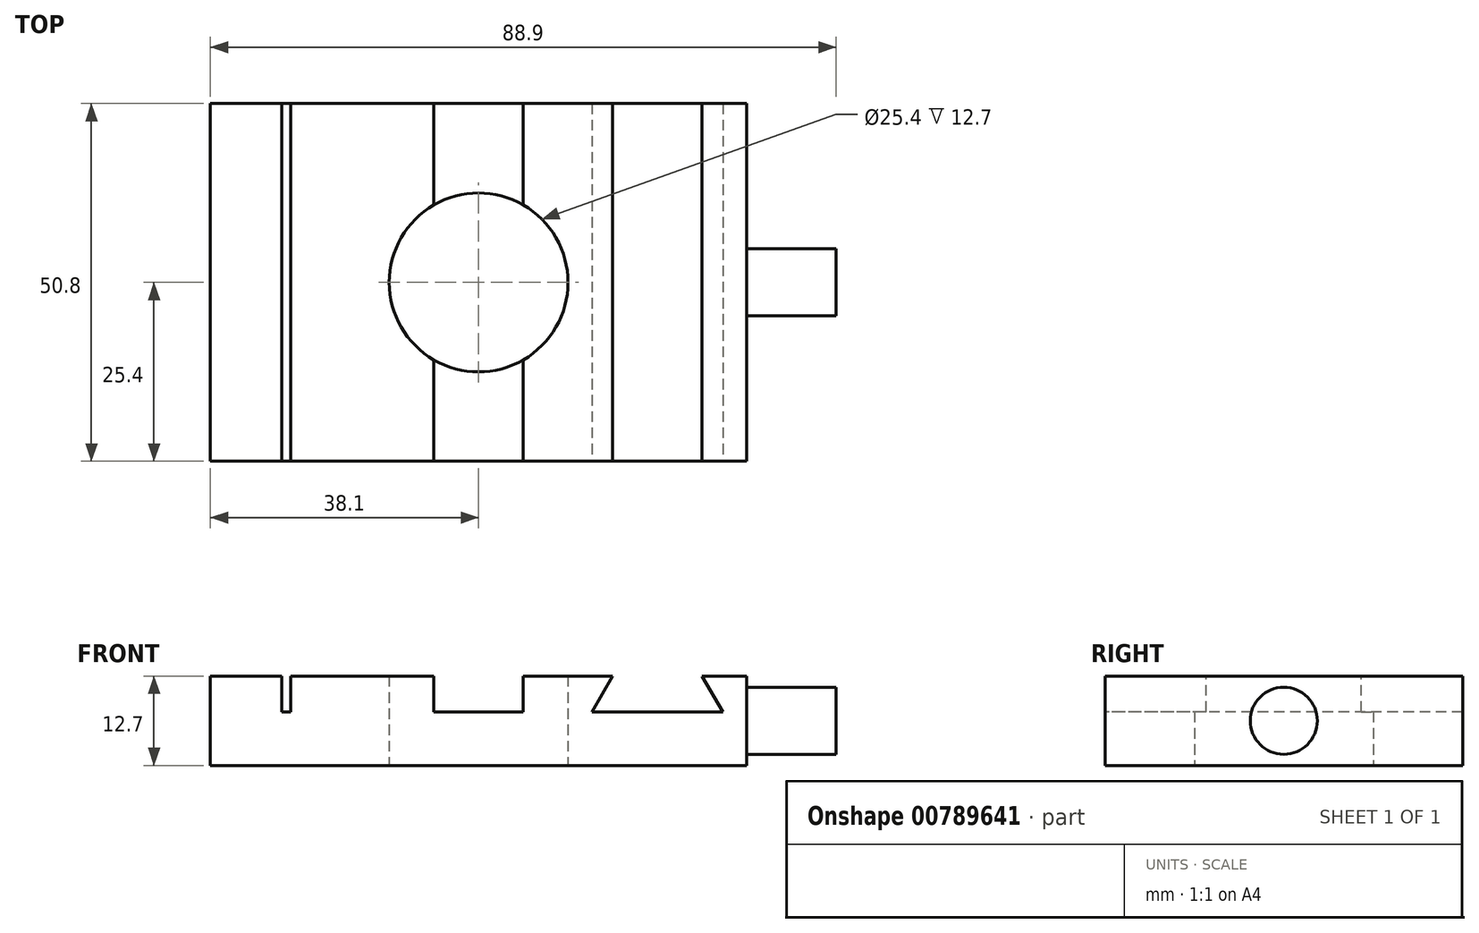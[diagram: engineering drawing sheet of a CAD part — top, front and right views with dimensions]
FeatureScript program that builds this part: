
annotation { "Feature Type Name" : "Feature", "Feature Type Description" : "" }
export const myFeature = defineFeature(function(context is Context, id is Id, definition is map)
    precondition{}
    {
        {
            var Q0;
            Q0=qCreatedBy(makeId("Top.planeOp"),FACE);
            var sketch = newSketch(context, id + "F0", { "sketchPlane" : qUnion([Q0])});
            skLineSegment(sketch, "E0.bottom", {"start": v(38.1, -25.4) * mm, "end": v(-38.1, -25.4) * mm});
            skLineSegment(sketch, "E0.top", {"start": v(38.1, 25.4) * mm, "end": v(-38.1, 25.4) * mm});
            skLineSegment(sketch, "E0.left", {"start": v(38.1, -25.4) * mm, "end": v(38.1, 25.4) * mm});
            skLineSegment(sketch, "E0.right", {"start": v(-38.1, -25.4) * mm, "end": v(-38.1, 25.4) * mm});
            skPoint(sketch, "E0.middle", {"position": v(0, 0) * mm});
            skCircle(sketch, "E1", {"center": v(0, 0) * mm, "radius": 12.7 * mm});
            skSolve(sketch);
        }
        {
            var Q0;
            Q0=makeQuery(id+"F0.imprint","IMPRINT",FACE,{"disambiguationData":[TD([[makeQuery(id+"F0.imprint","IMPRINT",EDGE,{"derivedFrom":sQuery(id+"F0.wireOp",EDGE,"E0.bottom")}),-1.0]])]});
            extrude(context, id + "F1", {"entities" : qUnion([Q0]), "depth" : 12.7 * mm, "offsetDistance" : 25.4 * mm});
        }
        {
            var Q0;
            Q0=makeQuery(id+"F1.opExtrude","CAP_FACE",FACE,{"disambiguationData":[OSD([sQuery(id+"F0.wireOp",EDGE,"E0.bottom"),sQuery(id+"F0.wireOp",EDGE,"E0.top"),sQuery(id+"F0.wireOp",EDGE,"E0.left"),sQuery(id+"F0.wireOp",EDGE,"E0.right"),sQuery(id+"F0.wireOp",EDGE,"E1")])],"isStart":false});
            var sketch = newSketch(context, id + "F2", { "sketchPlane" : qUnion([Q0])});
            skLineSegment(sketch, "E2.bottom", {"start": v(-27.94, 25.4) * mm, "end": v(-26.67, 25.4) * mm});
            skLineSegment(sketch, "E2.top", {"start": v(-27.94, -25.4) * mm, "end": v(-26.67, -25.4) * mm});
            skLineSegment(sketch, "E2.left", {"start": v(-27.94, 25.4) * mm, "end": v(-27.94, -25.4) * mm});
            skLineSegment(sketch, "E2.right", {"start": v(-26.67, 25.4) * mm, "end": v(-26.67, -25.4) * mm});
            skLineSegment(sketch, "E3.bottom", {"start": v(-6.35, 25.4) * mm, "end": v(6.35, 25.4) * mm});
            skLineSegment(sketch, "E3.top", {"start": v(-6.35, -25.4) * mm, "end": v(6.35, -25.4) * mm});
            skLineSegment(sketch, "E3.left", {"start": v(-6.35, 25.4) * mm, "end": v(-6.35, -25.4) * mm});
            skLineSegment(sketch, "E3.right", {"start": v(6.35, 25.4) * mm, "end": v(6.35, -25.4) * mm});
            skPoint(sketch, "E4", {"position": v(0, 0) * mm});
            skLineSegment(sketch, "E5", {"start": v(0, 25.4) * mm, "end": v(0, -25.4) * mm, "construction": true});
            skSolve(sketch);
        }
        {
            var Q0;
            Q0=makeQuery(id+"F2.imprint","IMPRINT",FACE,{"disambiguationData":[TD([[makeQuery(id+"F2.imprint","IMPRINT",EDGE,{"derivedFrom":sQuery(id+"F2.wireOp",EDGE,"E2.bottom")}),1.0]])]});
            var Q1;
            {var subQ0=sQuery(id+"F2.wireOp",EDGE,"E3.top");Q1=makeQuery(id+"F2.imprint","IMPRINT",FACE,{"disambiguationData":[TD([[makeQuery(id+"F2.imprint","IMPRINT",EDGE,{"derivedFrom":subQ0}),-1.0]])]});}
            var Q2;
            {var subQ0=sQuery(id+"F2.wireOp",EDGE,"E3.bottom");Q2=makeQuery(id+"F2.imprint","IMPRINT",FACE,{"disambiguationData":[TD([[makeQuery(id+"F2.imprint","IMPRINT",EDGE,{"derivedFrom":subQ0}),1.0]])]});}
            extrude(context, id + "F3", {"entities" : qUnion([Q0, Q1, Q2]), "operationType" : NewBodyOperationType.REMOVE, "oppositeDirection" : true, "depth" : 5.08 * mm, "offsetDistance" : 25.4 * mm});
        }
        {
            var Q0;
            Q0=makeQuery(id+"F1.opExtrude","SWEPT_FACE",FACE,{"disambiguationData":[OSD([sQuery(id+"F0.wireOp",EDGE,"E0.bottom")])]});
            var sketch = newSketch(context, id + "F4", { "sketchPlane" : qUnion([Q0])});
            skLineSegment(sketch, "E6", {"start": v(19.05, 12.7) * mm, "end": v(16.12, 7.62) * mm});
            skLineSegment(sketch, "E7", {"start": v(16.12, 7.62) * mm, "end": v(34.68, 7.62) * mm});
            skLineSegment(sketch, "E8", {"start": v(34.68, 7.62) * mm, "end": v(31.75, 12.7) * mm});
            skLineSegment(sketch, "E9", {"start": v(31.75, 12.7) * mm, "end": v(19.05, 12.7) * mm});
            skLineSegment(sketch, "E10", {"start": v(25.4, 7.62) * mm, "end": v(25.4, 12.7) * mm, "construction": true});
            skSolve(sketch);
        }
        {
            var Q0;
            Q0=makeQuery(id+"F4.imprint","IMPRINT",FACE,{"disambiguationData":[TD([[makeQuery(id+"F4.imprint","IMPRINT",EDGE,{"derivedFrom":sQuery(id+"F4.wireOp",EDGE,"E6")}),1.0]])]});
            extrude(context, id + "F5", {"entities" : qUnion([Q0]), "operationType" : NewBodyOperationType.REMOVE, "endBound" : BoundingType.THROUGH_ALL, "oppositeDirection" : true, "depth" : 25.4 * mm, "offsetDistance" : 25.4 * mm});
        }
        {
            var Q0;
            Q0=makeQuery(id+"F1.opExtrude","SWEPT_FACE",FACE,{"disambiguationData":[OSD([sQuery(id+"F0.wireOp",EDGE,"E0.left")])]});
            var sketch = newSketch(context, id + "F6", { "sketchPlane" : qUnion([Q0])});
            skCircle(sketch, "E11", {"center": v(0, 6.35) * mm, "radius": 4.76 * mm});
            skPoint(sketch, "E11.centerSnap0", {"position": v(-25.4, 6.35) * mm});
            skPoint(sketch, "E11.centerSnap1", {"position": v(0, 12.7) * mm});
            skSolve(sketch);
        }
        {
            var Q0;
            Q0=makeQuery(id+"F6.imprint","IMPRINT",FACE,{"disambiguationData":[TD([[makeQuery(id+"F6.imprint","IMPRINT",EDGE,{"derivedFrom":sQuery(id+"F6.wireOp",EDGE,"E11")}),1.0]])]});
            extrude(context, id + "F7", {"entities" : qUnion([Q0]), "operationType" : NewBodyOperationType.ADD, "depth" : 12.7 * mm, "offsetDistance" : 25.4 * mm});
        }
    });
